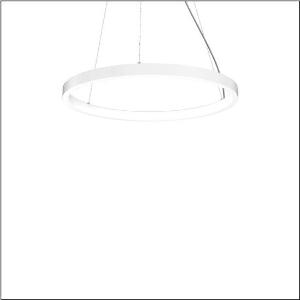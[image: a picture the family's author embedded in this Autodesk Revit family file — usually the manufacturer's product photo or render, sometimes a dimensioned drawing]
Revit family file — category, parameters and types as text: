
# Revit family: silica_r__21_ring-i_5pjbi3d1004a_d7a1
name_source: partatom
category: Lighting Fixtures
units: mm (PartAtom-declared; Revit-internal decimal feet)

## family parameters
Cut with Voids When Loaded = No
Host = Face
Light Source = No
Part Type = Normal
Room Calculation Point = No
Round Connector Dimension = Use Diameter
Shared = No

## types (1)
- Silica® 21 Ring-I (1 x LED, 6120 lm, 105 W, 3000K)
    Apparent Load = 105 VA
    CIE Flux Codes = 22 48 76 50 101
    Color Rendering = 80
    Color Temperature = 3000K
    Default Elevation = 1800 mm
    Description = Silica® 21 Ring-I, suspended luminaire, of PMMA, frosted, light emission: inner ring side luminous distribution, primary light characteristic: symmetric, installation type: suspended mounting, LED, rated luminous flux: 6.120lm, luminous efficacy: 58lm/W, light colour: 830, colour temperature: 3000K, with terminal, 5-pole, mains connection: 230V, AC/DC, 0/50..60Hz, rated input power: 105W, housing, of extruded aluminium section, traffic white (RAL 9016), diameter: 1.090mm, ceiling canopy, traffic white (RAL 9016), protection rating (lamp compartment): IP40, insulation class (complete): insulation class I (protective earthing), certification: CE, impact resistance: IK02, permissible operating ambient temperature: 0..+35°C, packaging unit: 1 piece
    Height = 48 mm  [stored 0.15748 ft]
    Lamp = 1 x LED
    Lamp Light Flux = 6120 lm
    Lamp Power = 105 W
    Lamp count = 1
    Length = 1090 mm
    Luminous efficacy = 58 lm/W
    Manufacturer = Siteco
    ModVariant = No
    Model = 5PJBI3D1004A
    Mounting Place = Ceiling
    Mounting Type = Pendant
    Number of Poles = 1
    OnlyDefault = Yes
    Power Factor = 1
    Product Name = Silica® 21 Ring-I
    Product group = suspended luminaire
    ProductGroupID = 904
    Protection Class = Protection class I
    Protection Degree = Degree of protection
    RLX_Detail_Level = 1
    RLX_Emergency_Light_Flux = 0 lm
    RLX_Emergency_Type = 0
    RLX_Emergency_Type_DB = No
    RlxData = <blob elided: 12777 chars, md5=1563c7ef>
    Socket = socket
    Standby Power = 0 W
    System Light Flux = 6120 lm
    System Power = 105 W
    Type Comments = Product without accessories
    Type Image = l_1258371.jpg
    URL = http://relux.com
    VarID = ---
    Voltage = 0 V
    Weight = 0.00 kg
    Width = 0 mm  [stored 0 ft]

note: [stored X ft] marks values corroborated as IEEE doubles in the binary element streams (Revit-internal decimal feet)

## geometry (parser evidence)
native form markers: Sweep x10
no freeform markers — native parametric forms only
